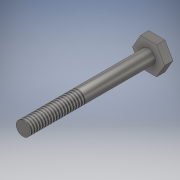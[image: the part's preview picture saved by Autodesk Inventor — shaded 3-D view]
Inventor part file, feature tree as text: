
AUTODESK INVENTOR PART (.ipt)
format: ipt  version: 2018 (Build 220112000, 112)  size: 111,104 bytes
history: native  units: in
note: dims shown in document units (in); Inventor stores cm internally (conversion verified against a paired STEP export)
features: extrude x2, sketch x2, thread x1
ambient origin geometry x8: Origin, YZ Plane, XZ Plane, XY Plane, X Axis, Y Axis, Z Axis, Center Point
bodies: Solid1 (feature_tree)
feature tree (5):
  extrude  "Extrusion1"  Depth=0.15in TaperAngle=0.0deg
  extrude  "Extrusion2"  Depth=2.25in TaperAngle=0.0deg
  thread  "Thread1"  [1 undecoded]
  sketch  "Sketch1"  dims[d0=0.5in d1=0.15in d2=0.0in]
  sketch  "Sketch2"  dims[d3=0.25in d4=2.25in d5=0.0in d6=1.0in d7=0.0in]
note: 1 required parameter value undecoded (feature->parameter linkage not recoverable at this tier; creation-order binding heuristic only, values carry confidence <= 0.55)
